# Revit family: QF_SANTOS_01P.181218024311
name_source: partatom
category: Specialty Equipment
revit_build: Autodesk Revit 2015 (Build: 20140903_1530(x64)
units: mm (PartAtom-declared; Revit-internal decimal feet)

## types (1)
- 01P_230V/1Ph/50Hz
    Accessory = No
    Apparent Power = 600 VA
    Conn Conduit = No
    Cycle = 50 Hz
    Depth Actual = 330 mm
    Description = PEPPER GRINDER WITH DRAWER 01P
    Electric power = 600 W
    FL Amps = 3 A
    Height Actual = 550 mm
    Length Actual = 210 mm  [stored 0.688976 ft]
    Manufacturer = SANTOS
    Max Overcurrent Protection = 0 A
    Min Ckt Ampacity = 0 A
    Model = 01P
    Number of Poles = 2
    Phase = 1
    Type Comments = Easy to use and efficient, this grinder will give you a high quality grinding. Grinding adjustments: from extra fine to extra coarse. Precision grinding: Ø 63,5 mm grinding dics which are designed and manufactured by Santos for a high quality grinding, precise and fine. Powerful: commercial reliable induction motor. Hopper: 1 Kg. Capacity of the plastic drawer: 800 g (1,8 lbs). Average output: 14 Kg / hour
    URL = www.santos.fr
    Volts = 230 V

note: [stored X ft] marks values corroborated as IEEE doubles in the binary element streams (Revit-internal decimal feet)

## geometry (parser evidence)
native form markers: Sweep x6
no freeform markers — native parametric forms only
